# Revit family: QF_BOURGEAT_silo_encastrable_modele_rond_assiettes310
name_source: partatom
category: Equipement spécialisé
revit_build: Autodesk Revit 2015 (Build: 20140606_1530(x64)
units: mm (PartAtom-declared; Revit-internal decimal feet)

## types (2) — shared parameters
Charge max = 80.00 kg
Fabricant = BOURGEAT
Hauteur hors tout = 883 mm  [stored 2.89698 ft]
Longueur hors tout = 428 mm  [stored 1.4042 ft]
Poids net à vide = 13.00 kg
Profondeur hors tout = 428 mm  [stored 1.4042 ft]
Spécification du Fabricant = SILO A NIVEAU CONSTANT ENCASTRABLE
URL catalogue = http://www.bourgeat.fr

## per-type parameters (varying)
| type | Fréquence | Indice de protection | Intensité nominale | Modèle | Phase | Puissance électrique  | Tension |
| silo_rond_assiettes310_chauffant_non_ventile | 50 Hz | 21 | 4 A | 777430 | 2 | 900 W | 230 V |
| silo_rond_assiettes310_neutre | 0 Hz |  | 0 A | 777433 | 0 | 0 W | 0 V |

note: [stored X ft] marks values corroborated as IEEE doubles in the binary element streams (Revit-internal decimal feet)
